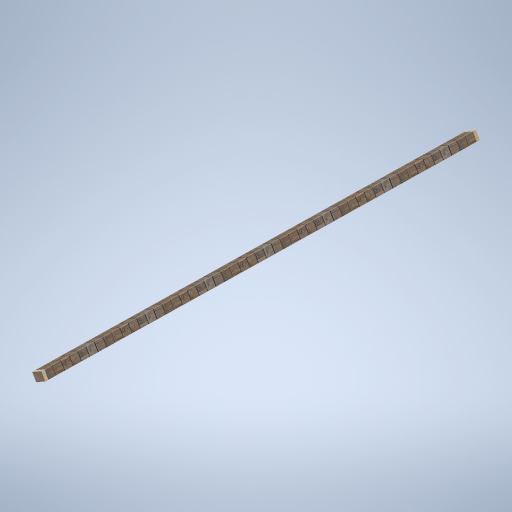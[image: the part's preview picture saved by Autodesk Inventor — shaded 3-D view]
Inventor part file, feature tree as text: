
AUTODESK INVENTOR PART (.ipt)
format: ipt  version: 2024.2 (Build 282272000, 272)  size: 308,224 bytes
history: native  units: mm
features: sketch x4, plane x2, extrude x2, projected_geometry x2, loft x1
ambient origin geometry x8: Origin, YZ Plane, XZ Plane, XY Plane, X Axis, Y Axis, Z Axis, Center Point
bodies: Solid1 (feature_tree)
feature tree (11):
  sketch  "Sketch1"  dims[d0=0.0mm d1=8101.0mm d2=0.0mm d3=90.0deg]
  plane  "Work Plane2"
  loft  "Loft1"
  sketch  "Sketch3"  dims[d8=50.0mm d9=0.0mm]
  sketch  "Sketch4"
  extrude  "Extrusion1"  Depth=50.0mm TaperAngle=0.0deg
  extrude  "Extrusion2"  [1 undecoded]
  plane  "Work Plane1"
  sketch  "Sketch2"  dims[d4=0.0mm d5=90.0deg d6=50.0mm d7=0.0mm]
  projected_geometry  "Projected Loop1"
  projected_geometry  "Projected Loop2"
note: 1 required parameter value undecoded (feature->parameter linkage not recoverable at this tier; creation-order binding heuristic only, values carry confidence <= 0.55)
